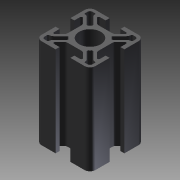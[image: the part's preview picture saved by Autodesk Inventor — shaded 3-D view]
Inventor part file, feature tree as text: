
AUTODESK INVENTOR PART (.ipt)
format: ipt  version: 2011 SP1 (Build 150282100, 282)  size: 223,744 bytes
history: native  units: mm
features: other x42, extrude x1, sketch x1
ambient origin geometry x8: Origin, YZ Plane, XZ Plane, XY Plane, X Axis, Y Axis, Z Axis, Center Point
bodies: Solid1 (feature_tree)
feature tree (44):
  extrude  "Extrusion1"  TaperAngle=0.0deg  [1 undecoded]
  other  "end_XY"
  other  "end_YZ"
  other  "end_ZX"
  other  "end_X"
  other  "end_Y"
  other  "end_Z"
  other  "end_Center"
  other  "side_1a_XY"
  other  "side_1a_YZ"
  other  "side_1a_ZX"
  other  "side_1a_X"
  other  "side_1a_Y"
  other  "side_1a_Z"
  other  "side_1a_Center"
  other  "side_2b_XY"
  other  "side_2b_YZ"
  other  "side_2b_ZX"
  other  "side_2b_X"
  other  "side_2b_Y"
  other  "side_2b_Z"
  other  "side_2b_Center"
  other  "side_3c_XY"
  other  "side_3c_YZ"
  other  "side_3c_ZX"
  other  "side_3c_X"
  other  "side_3c_Y"
  other  "side_3c_Z"
  other  "side_3c_Center"
  other  "side_4d_XY"
  other  "side_4d_YZ"
  other  "side_4d_ZX"
  other  "side_4d_X"
  other  "side_4d_Y"
  other  "side_4d_Z"
  other  "side_4d_Center"
  other  "start_XY"
  other  "start_YZ"
  other  "start_ZX"
  other  "start_X"
  other  "start_Y"
  other  "start_Z"
  other  "start_Center"
  sketch  "Skizze_1"  dims[d0=50.0mm d1=0.0mm d2=0.0mm d3=0.0mm]
note: 1 required parameter value undecoded (feature->parameter linkage not recoverable at this tier; creation-order binding heuristic only, values carry confidence <= 0.55)
